# Revit family: T200199
name_source: partatom
category: Furniture
revit_build: Autodesk Revit Architecture 2015 (Build: 20140322_1515(x64)
units: mm (PartAtom-declared; Revit-internal decimal feet)

## types (1)
- T200199
    Assembly Code = E2020400
    Catalog = https://ofs.com
    Description = OFS TYPICAL T200199
    Manufacturer = OFS
    Model = T200199
    Staks Box File Board = OFS STAKS Board Material
    Staks Box File Column = OFS STAKS Drawer Handle Metal
    Staks Box File Drawer Handle = OFS STAKS Drawer Handle Metal
    Staks Box File Leg Caps = OFS STAKS Leg Caps Material
    Staks Box File Top = OFS STAKS Board Material
    Staks Cross Rai Surface l = OFS STAKS Wood Grain Laminate Material
    Staks Cross Rail  Metal = OFS STAKS Power Jumper Conduit Material
    Staks Cross Rail Bracket = OFS STAKS Power Jumper Connector Material
    Staks Cross Rail Duplex Receptacle = OFS STAKS Power Jumper Connector Material
    Staks Cross Rail Power Block = OFS STAKS Power Block Material
    Staks Cross Rail Power Block Casing = OFS STAKS Power Block Casing Material
    Staks Cushion = OFS STAKS Cushion Material
    Staks Height Workgroup Board = OFS STAKS Board Material
    Staks Height Workgroup Column = OFS STAKS Column Material
    Staks Height Workgroup Leg Caps = OFS STAKS Leg Caps Material
    Staks Height Workgroup top = OFS STAKS Board Material
    Staks Height Worksuface  3d Laminate = OFS STAKS Laminate Material
    Staks Height Worksuface Edge = OFS STAKS Edge Material
    Staks Height Worksuface Venner = OFS STAKS Surface Material
    Staks Wire Manager = OFS STAKS PET Wire Manager Material
    Staks Worksuface Edge Panel = OFS STAKS Frosted Glass
    URL = https://ofs.com

## geometry (parser evidence)
native form markers: Blend x68, Sweep x26
no freeform markers — native parametric forms only
